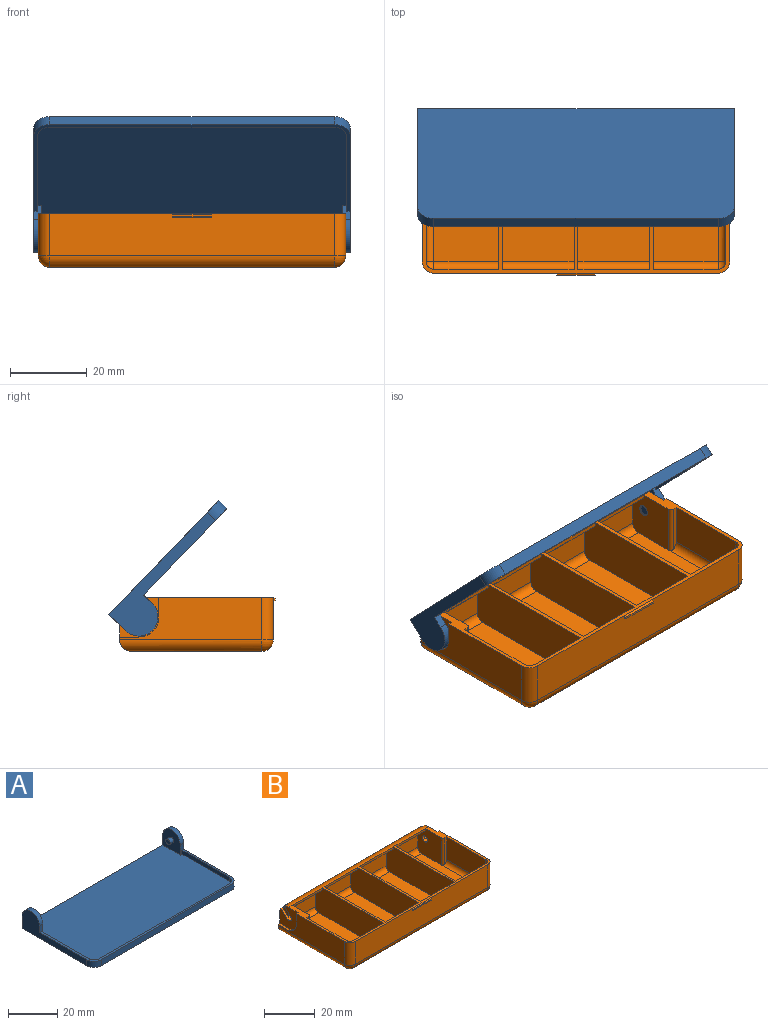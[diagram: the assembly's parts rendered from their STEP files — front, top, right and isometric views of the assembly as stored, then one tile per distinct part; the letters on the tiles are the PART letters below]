
ASSEMBLY  parts=2 mates=1
PART A: 28 faces, bbox 82.5x41.3x11 mm
  f0: plane 80.5x40.75mm, normal (0,0,1), area 3223.1mm2, adj f2,f9,f10,f11,f12,f13,f14,f16
  f1: plane 82.5x31.25mm, normal (0,0,1), area 139.8mm2, adj f2,f3,f4,f5,f7,f8,f9,f10
  f2: plane 27x2mm, normal (-1,0,0), area 54mm2, adj f0,f1,f12,f14
  f3: plane 37x11mm, normal (1,0,0), area 180.3mm2, adj f1,f6,f8,f13,f14,f15
  f4: plane 37x11mm, normal (-1,0,0), area 180.3mm2, adj f1,f6,f7,f13,f19,f20
  f5: plane 74x3mm, normal (0,-1,0), area 222mm2, adj f1,f6,f7,f8
  f6: plane 82.5x41.25mm, normal (0,0,-1), area 3395.4mm2, adj f3,f4,f5,f7,f8,f13
  f7: cylinder r=4.25mm len=4.25mm, axis (0,0,-1), area 20mm2, adj f1,f4,f5,f6
  f8: cylinder r=4.25mm len=4.25mm, axis (0,0,1), area 20mm2, adj f1,f3,f5,f6
  f9: plane 27x2mm, normal (1,0,0), area 54mm2, adj f0,f1,f11,f19
  f10: plane 74x2mm, normal (0,1,0), area 131.5mm2, adj f0,f1,f11,f12,f25,f26,f27
  f11: cylinder r=3.25mm len=3.25mm, axis (0,0,-1), area 10.2mm2, adj f0,f1,f9,f10
  f12: cylinder r=3.25mm len=3.25mm, axis (0,0,1), area 10.2mm2, adj f0,f1,f2,f10
  f13: plane 82.5x6mm, normal (0,1,0), area 102.5mm2, adj f0,f3,f4,f6,f15,f16,f20,f21
  f14: plane 5x2mm, normal (0,-1,0), area 8mm2, adj f0,f1,f2,f3,f15,f16
  f15: cylinder r=5mm len=10mm, axis (1,0,0), area 31.4mm2, adj f3,f13,f14,f16
  f16: plane 10x10mm, normal (-1,0,0), area 84.4mm2, adj f0,f13,f14,f15,f17
  f17: cylinder r=1.25mm len=2.5mm, axis (1,0,0), area 15.7mm2, adj f16,f18
  f18: plane 2.5x2.5mm, normal (-1,0,0), area 4.9mm2, adj f17
  f19: plane 5x2mm, normal (0,-1,0), area 8mm2, adj f0,f1,f4,f9,f20,f21
  f20: cylinder r=5mm len=10mm, axis (-1,0,0), area 31.4mm2, adj f4,f13,f19,f21
  f21: plane 10x10mm, normal (1,0,0), area 84.4mm2, adj f0,f13,f19,f20,f22
  f22: cylinder r=1.25mm len=2.5mm, axis (-1,0,0), area 15.7mm2, adj f21,f23
  f23: plane 2.5x2.5mm, normal (1,0,0), area 4.9mm2, adj f22
  f24: plane 15x0.6mm, normal (0,1,0), area 9mm2, adj f0,f25,f26,f27
  f25: plane 1.1x0.5mm, normal (1,0,0), area 0.4mm2, adj f0,f10,f24,f27
  f26: plane 1.1x0.5mm, normal (-1,0,0), area 0.4mm2, adj f0,f10,f24,f27
  f27: plane 15x0.5mm, normal (0,0.71,-0.71), area 10.6mm2, adj f10,f24,f25,f26
PART B: 86 faces, bbox 80x40.5x14 mm
  f0: cylinder r=5mm len=78mm, axis (1,0,0), area 604.1mm2, adj f2,f3,f4,f5,f7,f14,f22,f31
  f1: cylinder r=1.4mm len=2.8mm, axis (1,0,0), area 13.2mm2, adj f2,f58,f79,f80,f81
  f2: plane 10.25x10.25mm, normal (-1,0,0), area 76.9mm2, adj f0,f1,f4,f5,f73,f74,f75,f80
  f3: plane 10.25x10.25mm, normal (1,0,0), area 76.9mm2, adj f0,f4,f5,f6,f70,f71,f72,f76
  f4: plane 80x35mm, normal (0,0,1), area 276.9mm2, adj f0,f2,f3,f8,f15,f23,f28,f32
  f5: plane 80x6mm, normal (0,1,0), area 469.5mm2, adj f0,f2,f3,f35,f36,f42,f72,f75
  f6: cylinder r=1.4mm len=2.8mm, axis (1,0,0), area 13.2mm2, adj f3,f56,f76,f77,f78
  f7: plane 16.75x1mm, normal (0,-1,0), area 16.8mm2, adj f0,f12,f58,f64
  f8: plane 16.75x11mm, normal (0,1,0), area 184.2mm2, adj f4,f13,f54,f64
  f9: plane 18.75x6mm, normal (0,-1,0), area 112.5mm2, adj f18,f19,f62,f63
  f10: plane 34x18.75mm, normal (0,0,1), area 637.5mm2, adj f18,f20,f62,f63
  f11: cylinder r=2mm len=16.75mm, axis (-1,0,0), area 52.6mm2, adj f29,f48,f58,f64
  f12: cylinder r=4mm len=16.75mm, axis (1,0,0), area 105.2mm2, adj f7,f29,f58,f64
  f13: cylinder r=2mm len=16.75mm, axis (1,0,0), area 52.6mm2, adj f8,f48,f53,f64
  f14: plane 18.75x1mm, normal (0,-1,0), area 18.8mm2, adj f0,f19,f62,f63
  f15: plane 18.75x11mm, normal (0,1,0), area 206.2mm2, adj f4,f20,f62,f63
  f16: plane 18.75x6mm, normal (0,-1,0), area 112.5mm2, adj f25,f26,f60,f61
  f17: plane 34x18.75mm, normal (0,0,1), area 637.5mm2, adj f25,f27,f60,f61
  f18: cylinder r=2mm len=18.75mm, axis (-1,0,0), area 58.9mm2, adj f9,f10,f62,f63
  f19: cylinder r=4mm len=18.75mm, axis (1,0,0), area 117.8mm2, adj f9,f14,f62,f63
  f20: cylinder r=2mm len=18.75mm, axis (1,0,0), area 58.9mm2, adj f10,f15,f62,f63
  f21: plane 16.75x6mm, normal (0,-1,0), area 100.5mm2, adj f33,f34,f56,f59
  f22: plane 18.75x1mm, normal (0,-1,0), area 18.8mm2, adj f0,f26,f60,f61
  f23: plane 18.75x11mm, normal (0,1,0), area 206.2mm2, adj f4,f27,f60,f61
  f24: plane 34x16.75mm, normal (0,0,1), area 569.5mm2, adj f33,f50,f52,f56,f59
  f25: cylinder r=2mm len=18.75mm, axis (-1,0,0), area 58.9mm2, adj f16,f17,f60,f61
  f26: cylinder r=4mm len=18.75mm, axis (1,0,0), area 117.8mm2, adj f16,f22,f60,f61
  f27: cylinder r=2mm len=18.75mm, axis (1,0,0), area 58.9mm2, adj f17,f23,f60,f61
  f28: plane 22x11mm, normal (1,0,0), area 242mm2, adj f4,f30,f54,f57
  f29: plane 16.75x6mm, normal (0,-1,0), area 100.5mm2, adj f11,f12,f58,f64
  f30: cylinder r=2mm len=23mm, axis (0,-1,0), area 69.3mm2, adj f28,f48,f53,f57,f84
  f31: plane 16.75x1mm, normal (0,-1,0), area 16.8mm2, adj f0,f34,f56,f59
  f32: plane 22x11mm, normal (-1,0,0), area 242mm2, adj f4,f49,f50,f55
  f33: cylinder r=2mm len=16.75mm, axis (-1,0,0), area 52.6mm2, adj f21,f24,f56,f59
  f34: cylinder r=4mm len=16.75mm, axis (1,0,0), area 105.2mm2, adj f21,f31,f56,f59
  f35: plane 37x11mm, normal (-1,0,0), area 307.9mm2, adj f4,f5,f44,f46,f73,f74,f75
  f36: plane 37x11mm, normal (1,0,0), area 307.9mm2, adj f4,f5,f39,f40,f70,f71,f72
  f37: plane 74x11mm, normal (0,-1,0), area 804mm2, adj f4,f39,f43,f46,f65,f68,f69
  f38: plane 74x34mm, normal (0,0,-1), area 2516mm2, adj f40,f42,f43,f44
  f39: cylinder r=3mm len=11mm, axis (0,0,1), area 51.8mm2, adj f4,f36,f37,f41
  f40: cylinder r=3mm len=37mm, axis (0,1,0), area 169.2mm2, adj f36,f38,f41,f42
  f41: sphere r=3mm, area 14.1mm2, adj f39,f40,f43
  f42: cylinder r=3mm len=80mm, axis (-1,0,0), area 366.7mm2, adj f5,f38,f40,f44
  f43: cylinder r=3mm len=74mm, axis (1,0,0), area 348.7mm2, adj f37,f38,f41,f45
  f44: cylinder r=3mm len=37mm, axis (0,-1,0), area 169.2mm2, adj f35,f38,f42,f45
  f45: sphere r=3mm, area 14.1mm2, adj f43,f44,f46
  f46: cylinder r=3mm len=11mm, axis (0,0,-1), area 51.8mm2, adj f4,f35,f37,f45
  f47: plane 16.75x11mm, normal (0,1,0), area 184.2mm2, adj f4,f49,f52,f59
  f48: plane 34x16.75mm, normal (0,0,1), area 569.5mm2, adj f11,f13,f30,f58,f64
  f49: cylinder r=2mm len=11mm, axis (0,0,1), area 34.6mm2, adj f4,f32,f47,f51
  f50: cylinder r=2mm len=23mm, axis (0,1,0), area 69.3mm2, adj f24,f32,f51,f55,f85
  f51: sphere r=2mm, area 6.3mm2, adj f49,f50,f52
  f52: cylinder r=2mm len=16.75mm, axis (1,0,0), area 52.6mm2, adj f24,f47,f51,f59
  f53: sphere r=2mm, area 6.3mm2, adj f13,f30,f54
  f54: cylinder r=2mm len=11mm, axis (0,0,-1), area 34.6mm2, adj f4,f8,f28,f53
  f55: plane 12.73x1mm, normal (0,-1,0), area 12.2mm2, adj f4,f32,f50,f85
  f56: plane 13x13mm, normal (-1,0,0), area 154.6mm2, adj f4,f6,f21,f24,f31,f33,f34,f85
  f57: plane 12.73x1mm, normal (0,-1,0), area 12.2mm2, adj f4,f28,f30,f84
  f58: plane 13x13mm, normal (1,0,0), area 154.6mm2, adj f1,f4,f7,f11,f12,f29,f48,f84
  f59: plane 38x13mm, normal (1,0,0), area 484.8mm2, adj f4,f21,f24,f31,f33,f34,f47,f52
  f60: plane 38x13mm, normal (-1,0,0), area 484.8mm2, adj f4,f16,f17,f22,f23,f25,f26,f27
  f61: plane 38x13mm, normal (1,0,0), area 484.8mm2, adj f4,f16,f17,f22,f23,f25,f26,f27
  f62: plane 38x13mm, normal (-1,0,0), area 484.8mm2, adj f4,f9,f10,f14,f15,f18,f19,f20
  f63: plane 38x13mm, normal (1,0,0), area 484.8mm2, adj f4,f9,f10,f14,f15,f18,f19,f20
  f64: plane 38x13mm, normal (-1,0,0), area 484.8mm2, adj f4,f7,f8,f11,f12,f13,f29,f48
  f65: plane 10x0.5mm, normal (0,-0.45,-0.89), area 5.6mm2, adj f37,f67,f68,f69
  f66: plane 10x0.5mm, normal (0,-0.45,0.89), area 5.6mm2, adj f4,f67,f68,f69
  f67: plane 10x0.5mm, normal (0,-1,0), area 5mm2, adj f65,f66,f68,f69
  f68: plane 1x0.5mm, normal (1,0,0), area 0.4mm2, adj f37,f65,f66,f67
  f69: plane 1x0.5mm, normal (-1,0,0), area 0.4mm2, adj f37,f65,f66,f67
  f70: plane 5x1mm, normal (0,1,0), area 5mm2, adj f3,f4,f36,f71
  f71: cylinder r=5.25mm len=5.25mm, axis (1,0,0), area 8.2mm2, adj f3,f36,f70,f72
  f72: plane 5x1mm, normal (0,0,1), area 5mm2, adj f3,f5,f36,f71
  f73: cylinder r=5.25mm len=5.25mm, axis (-1,0,0), area 8.2mm2, adj f2,f35,f74,f75
  f74: plane 5x1mm, normal (0,1,0), area 5mm2, adj f2,f4,f35,f73
  f75: plane 5x1mm, normal (0,0,1), area 5mm2, adj f2,f5,f35,f73
  f76: plane 3.39x3.39mm, normal (0,0.71,-0.71), area 4.9mm2, adj f0,f3,f6,f78,f83
  f77: plane 3.39x3.39mm, normal (0,-0.71,0.71), area 4.9mm2, adj f0,f3,f6,f78,f83
  f78: plane 5x5mm, normal (1,0,0), area 9.3mm2, adj f6,f76,f77,f83
  f79: plane 5x5mm, normal (-1,0,0), area 9.3mm2, adj f1,f80,f81,f82
  f80: plane 3.39x3.39mm, normal (0,0.71,-0.71), area 4.9mm2, adj f0,f1,f2,f79,f82
  f81: plane 3.39x3.39mm, normal (0,-0.71,0.71), area 4.9mm2, adj f0,f1,f2,f79,f82
  f82: torus R=4.5mm, axis (-1,0,0), area 2.2mm2, adj f0,f79,f80,f81
  f83: torus R=4.5mm, axis (1,0,0), area 2.2mm2, adj f0,f76,f77,f78
  f84: cylinder r=1mm len=13mm, axis (0,0,1), area 20.3mm2, adj f4,f30,f57,f58
  f85: cylinder r=1mm len=13mm, axis (0,0,-1), area 20.3mm2, adj f4,f50,f55,f56
PLACE A rot(axis=(0,-0.92,0.39),180deg) t=(-19.53,-0.85,19.23)mm
PLACE B t=(-19.53,-9.77,-4.74)mm fixed
MATE revolute B.f83 <-> A.f17  axis (1,0,0) through (19.47,5.23,4.26)mm
